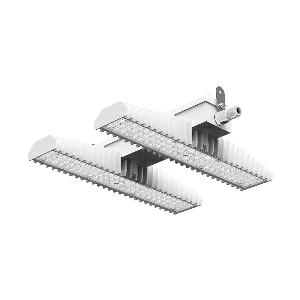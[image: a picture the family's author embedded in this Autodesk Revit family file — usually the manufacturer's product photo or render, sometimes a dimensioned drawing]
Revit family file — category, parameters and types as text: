
# Revit family: 3f_filippi_-_3f_lem_ho_ampio_3f_filippi_-_58954_-_3f_lem_2_ho_led_140_cr_ampio
name_source: partatom
category: Lighting Fixtures
units: mm (PartAtom-declared; Revit-internal decimal feet)

## family parameters
Cut with Voids When Loaded = No
Host = Face
Light Source = No
Part Type = Normal
Room Calculation Point = No
Round Connector Dimension = Use Diameter
Shared = No

## types (1)
- 3F Filippi - 3F LEM HO Ampio (1 x LED, 22606 lm, 138 W, 4000 K)
    Apparent Load = 138 VA
    Approval mark = CE
    CIE Flux Codes = 60 92 99 100 100
    Color Rendering = 80
    Color Temperature = 4000 K
    Control Gear = Electronic ballast
    Default Elevation = 1800 mm
    Description = Industrial luminaire with high light output and high luminous efficiency designed with the most innovative technologies for environments with temperature up to 55°C.

ILLUMINOTECHNICAL
Luminous efficiency 100% (DLOR 100%, ULOR 0%).
Initial luminous flux of the luminaire 22606 lm.
Direct symmetric wide distribution: the illuminated area has a rectangular shape.
Installation Interdistance Transv.D = 1.58 x hu - Long.D = 1.45 x hu.
Tabular UGR (CIE 117 - 4H-8H; S=0.25H; 70/50/20): RUG 23.5 - 24.5.
Beam angle: 93° - 99°.
Luminous efficacy 164 lm/W.
Lifetime (L93/B10): 30000 h. (tq+25°C)
Lifetime (L90/B10): 50000 h. (tq+25°C)
Lifetime (L85/B10): 80000 h. (tq+25°C)
Lifetime (L80/B10): 100000 h. (tq+25°C)
Lifetime (L85/B10): 50000 h. (tq+55°C)
Sudden decreased luminous flux after 50000 hours: 0% (C0).
Photobiological safety in compliance with IEC/TR 62778: RG0 risk exempt, (IEC 62471).
In compliance with IEC/EN 62722-2-1 - IEC/EN 62717 standards.

SOURCE
2 Mid-Power linear LED modules 70W/840.
Energy efficiency class (UE 2019/2020 - UE 2019/2015): C.
CIE 13.3 Colour rendering index: CRI >80 (R9 <50%).
IES TM-30 Fidelity Index: Rf = 84 Rg = 95.
CCT nominal colour temperature 4000 K.
Colour initial tolerance (MacAdam): SDCM 3.

MECHANICAL
Passive modular heatsinks in die-casted aluminium, painted in white colour.
To optimize the thermal management of the LED module, the heatsinks are oversized and provided with self-cleaning of cooling fins.
Wiring body in aluminium and galvanised steel anchored solidly to the sinks and thermally separated.
3F Lens lenses with high luminous efficiency, transparent methacrylate (PMMA), fixed to the LED modules.
Fixing brackets in stainless steel.
Luminaire with limited surface temperature. - D - (EN 60598-2-24)
Dimensions: 470x542 mm, height 129 mm. Weight 9.165 kg.
IP65 protection degree.
Mechanical strength to impacts IK06 (1 joule).
Glow-wire test resistance 650°C.

ELECTRICAL
Halogen Free electronic wiring 230V-50/60Hz, power factor 0.97, THD <25%, constant output current, class I, 1 driver.
Power of the luminaire 138 W.
ENEC - CE.
SAFE FLICKER: PstLM=<1 and SVM=<0.4 (IEC TR 61547-1 and IEC TR 63158), to ensure a more comfortable and safe light.
Luminaire compliant with EN 60598-2-22 for power supply from a centralised emergency system CPSS (Central Power Supply System), not incorporated in the luminaire - high risk areas excluded. The default power and flux are 100% in AC and 100% in DC.
Ambient temperature from -30°C to +55°C.
Temperature class T6 max 85°C.
Quick connection via M20 3P connector with 9-13 mm tightening range.
Power unit positioned on a separate compartment by the LED module to ensure optimum temperatures of cabling components, to be inspectable and maintainable.
Relative humidity UR: <85%.

INSTALLATION
Ceiling / Suspended / Wall.
All accessories dedicated to this product are available on the Catalog and on our website www.3F-Filippi.com.

APPLICATIONS
In commercial environments, exhibition and industrial areas, stores, open areas.
Environments in which it is necessary a total protection against falling fragments (eg environments with foodstuffs or machines with moving parts or with extreme temperature changes), use luminaires with polycarbonate lenses.

WARNING
Fixture not suitable for cold stores with an ambient temperature <0°C and/or relative humidity >85%.
Luminaire designed for disposal/recycling at end-of-life.
Replaceable (LED only) light source by a professional. Replaceable control gear by a professional.
    Height = 129 mm
    Lamp = 1 x LED
    Lamp Light Flux = 22606 lm
    Lamp Power = 138 W
    Lamp count = 1
    Length = 470 mm
    Lifetime = 50000 h
    Luminous efficacy = 164 lm/W
    Manufacturer = 3F Filippi
    ModVariant = No
    Model = 3F Filippi - 58954 - 3F LEM 2 HO LED 140 CR AMPIO
    Mounting Place = Ceiling
    Mounting Type = Pendant
    Number of Poles = 1
    OnlyDefault = Yes
    Power Factor = 1
    Product Name = 3F Filippi - 3F LEM HO Ampio
    Product group = pendant luminaire
    ProductGroupID = 9
    Protection Class = Protection class I
    Protection Degree = IP 65
    RLX_Detail_Level = 1
    RLX_Emergency_Light_Flux = 0 lm
    RLX_Emergency_Type = 0
    RLX_Emergency_Type_DB = No
    RlxData = <blob elided: 96177 chars, md5=6fb41126>
    Socket = socket
    Standby Power = 0 W
    System Light Flux = 22606 lm
    System Power = 138 W
    Type Comments = Product without accessories
    Type Image = 3f_filippi_-_lem_2.jpg
    URL = http://relux.com
    VarID = ---
    Voltage = 0 V
    Weight = 0.00 kg
    Width = 542 mm

## geometry (parser evidence)
native form markers: Blend x4, Sweep x12
no freeform markers — native parametric forms only
